# Revit family: Volta-IP30-Flush_mounted-syst-NoHosted-BE-fr
name_source: partatom
category: Electrical Equipment
units: mm (PartAtom-declared; Revit-internal decimal feet)

## family parameters
Always vertical = Yes
Cut with Voids When Loaded = No
Panel Configuration = Two Columns, Circuits Across
Part Type = Panelboard
Room Calculation Point = No
Round Connector Dimension = Use Diameter
Shared = No
Work Plane-Based = Yes

## types (9) — shared parameters
Default Elevation = 1219 mm
EF000003 - mode de pose = EV000383 - encastré
EF000007 - couleur = EV000202 - blanc
EF000008 - largeur = 348 mm  [stored 1.14173 ft]
EF000049 - profondeur = 98 mm  [stored 0.321522 ft]
EF000116 - numéro RAL = 9010
EF000218 - profondeur d'encastrement = 89 mm  [stored 0.291995 ft]
EF000339 - type de capot = EV004216 - porte
EF000846 - largeur d'encastrement = 314 mm  [stored 1.03018 ft]
EF001062 - finition CEM = No
EF001088 - possibilité de montage en saillie = Yes
EF001131 - profondeur intérieure = 92 mm
EF001134 - rail DIN = Yes
EF001596 - matériau du boîtier/corps = EV000139 - plastique
EF002950 - largeur en nombre de modules = 12
EF004462 - type de fermeture = EV000154 - autre
EF005474 - indice de protection (IP) = EV006410 - IP30
EF006244 - couvercle/porte transparent(e) = No
EF006306 - avec serrure = No
EF009212 - finition du couvercle = EV009916 - avec échancrure
EF015776 - borne de mise à la terre = No
EF015777 - borne à conducteur neutre = No
EF015941 - porte pour transmission du signal = No
HG000001 - nombre de colonnes = 1
HG000002 - avec porte = Yes
HG000003 - Gamme = Volta
HG000005 - Epaisseur = 3 mm  [stored 0.00984252 ft]
HG000006 - encastré = Yes
HG000009 - Porte à double battant = No
HG000010 - Portes asymétriques = No
HG000011 - Rangées du bas vides = No
Manufacturer = Hager
Type Comments = Volta
zero-valued in all types: HG000007 - Nombre de colonnes vides, HG000008 - Nombre de rangées vides

## per-type parameters (varying)
| type | EF000040 - hauteur | EF000118 - avec cadre/support de montage | EF000266 - nombre de rangées | EF000332 - hauteur d'encastrement | HG000004 - Référence fabricant | Model |
| Encastré IP30 L348 H356.5 P98 12 Modules - VU12LN | 356 mm | Yes | 1 | 321 mm | VU12LN | VU12LN |
| Encastré IP30 L348 H356.5 P98 12 Modules - VU12NC | 356 mm | No | 1 | 321 mm | VU12NC | VU12NC |
| Encastré IP30 L348 H505.5 P98 12 Modules - VU24LN | 506 mm | Yes | 2 | 470 mm | VU24LN | VU24LN |
| Encastré IP30 L348 H505.5 P98 12 Modules - VU24NC | 506 mm | No | 2 | 470 mm | VU24NC | VU24NC |
| Encastré IP30 L348 H630.5 P98 12 Modules - VU36LN | 630 mm | Yes | 3 | 595 mm | VU36LN | VU36LN |
| Encastré IP30 L348 H630.5 P98 12 Modules - VU36NC | 630 mm | No | 3 | 595 mm | VU36NC | VU36NC |
| Encastré IP30 L348 H755.5 P98 12 Modules - VU48LN | 756 mm | Yes | 4 | 720 mm | VU48LN | VU48LN |
| Encastré IP30 L348 H755.5 P98 12 Modules - VU48NC | 756 mm | No | 4 | 720 mm | VU48NC | VU48NC |
| Encastré IP30 L348 H880.5 P98 12 Modules - VU60NC | 880 mm  [stored 2.88714 ft] | No | 5 | 845 mm  [stored 2.77231 ft] | VU60NC | VU60NC |

note: [stored X ft] marks values corroborated as IEEE doubles in the binary element streams (Revit-internal decimal feet)

## geometry (parser evidence)
native form markers: Sweep x14
no freeform markers — native parametric forms only
